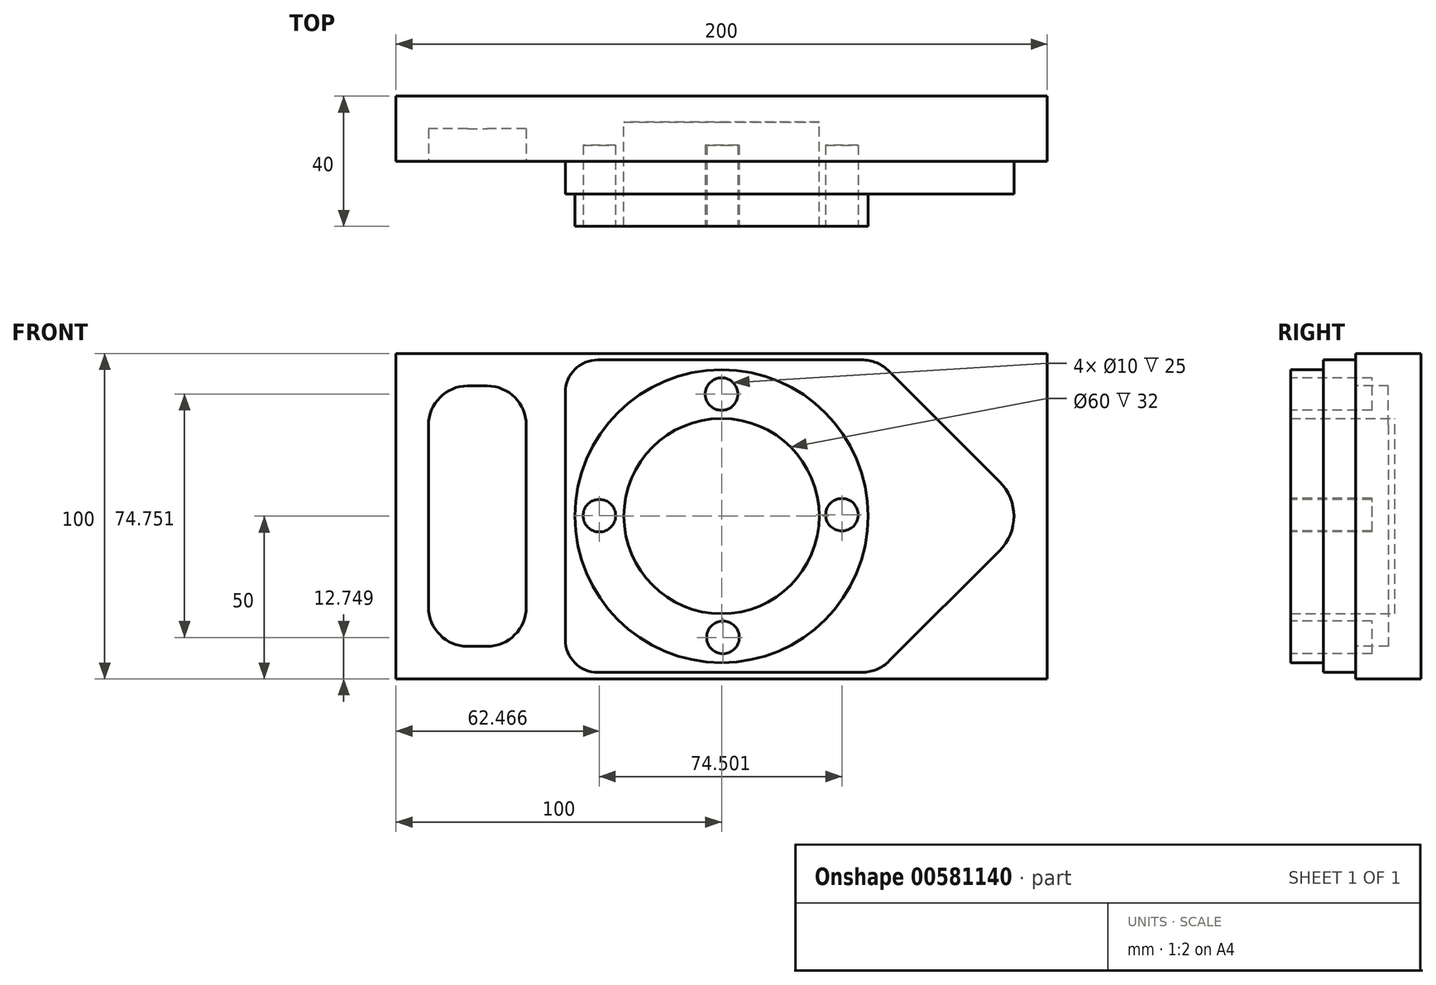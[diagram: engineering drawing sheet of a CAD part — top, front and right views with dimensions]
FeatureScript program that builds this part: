
annotation { "Feature Type Name" : "Feature", "Feature Type Description" : "" }
export const myFeature = defineFeature(function(context is Context, id is Id, definition is map)
    precondition{}
    {
        {
            var Q0;
            Q0=qCreatedBy(makeId("Front.planeOp"),FACE);
            var sketch = newSketch(context, id + "F0", { "sketchPlane" : qUnion([Q0])});
            skLineSegment(sketch, "E0.bottom", {"start": v(-100, 50) * mm, "end": v(100, 50) * mm});
            skLineSegment(sketch, "E0.top", {"start": v(-100, -50) * mm, "end": v(100, -50) * mm});
            skLineSegment(sketch, "E0.left", {"start": v(-100, 50) * mm, "end": v(-100, -50) * mm});
            skLineSegment(sketch, "E0.right", {"start": v(100, 50) * mm, "end": v(100, -50) * mm});
            skPoint(sketch, "E0.middle", {"position": v(0, 0) * mm});
            skSolve(sketch);
        }
        {
            var Q0;
            Q0=makeQuery(id+"F0.imprint","IMPRINT",FACE,{"disambiguationData":[TD([[makeQuery(id+"F0.imprint","IMPRINT",EDGE,{"derivedFrom":sQuery(id+"F0.wireOp",EDGE,"E0.bottom")}),-1.0]])]});
            extrude(context, id + "F1", {"entities" : qUnion([Q0]), "depth" : 20 * mm, "offsetDistance" : 25 * mm});
        }
        {
            var Q0;
            Q0=makeQuery(id+"F1.opExtrude","CAP_FACE",FACE,{"disambiguationData":[OSD([sQuery(id+"F0.wireOp",EDGE,"E0.bottom"),sQuery(id+"F0.wireOp",EDGE,"E0.top"),sQuery(id+"F0.wireOp",EDGE,"E0.left"),sQuery(id+"F0.wireOp",EDGE,"E0.right")])],"isStart":false});
            var sketch = newSketch(context, id + "F2", { "sketchPlane" : qUnion([Q0])});
            skLineSegment(sketch, "E1.bottom", {"start": v(-78, 40) * mm, "end": v(-72, 40) * mm});
            skLineSegment(sketch, "E1.top", {"start": v(-78, -40) * mm, "end": v(-72, -40) * mm});
            skLineSegment(sketch, "E1.left", {"start": v(-90, 28) * mm, "end": v(-90, -28) * mm});
            skLineSegment(sketch, "E1.right", {"start": v(-60, 28) * mm, "end": v(-60, -28) * mm});
            skPoint(sketch, "E1.middle", {"position": v(-75, 0) * mm});
            skPoint(sketch, "E2.visualSharp", {"position": v(-90, 40) * mm});
            skArc(sketch, "E2.filletArc", {"start": v(-78, 40) * mm, "mid": v(-86.49, 36.49) * mm, "end": v(-90, 28) * mm});
            skPoint(sketch, "E3.visualSharp", {"position": v(-60, 40) * mm});
            skArc(sketch, "E3.filletArc", {"start": v(-60, 28) * mm, "mid": v(-63.51, 36.49) * mm, "end": v(-72, 40) * mm});
            skPoint(sketch, "E4.visualSharp", {"position": v(-60, -40) * mm});
            skArc(sketch, "E4.filletArc", {"start": v(-72, -40) * mm, "mid": v(-63.51, -36.49) * mm, "end": v(-60, -28) * mm});
            skPoint(sketch, "E5.visualSharp", {"position": v(-90, -40) * mm});
            skArc(sketch, "E5.filletArc", {"start": v(-90, -28) * mm, "mid": v(-86.49, -36.49) * mm, "end": v(-78, -40) * mm});
            skSolve(sketch);
        }
        {
            var Q0;
            Q0=makeQuery(id+"F2.imprint","IMPRINT",FACE,{"disambiguationData":[TD([[makeQuery(id+"F2.imprint","IMPRINT",EDGE,{"derivedFrom":sQuery(id+"F2.wireOp",EDGE,"E1.bottom")}),-1.0]])]});
            extrude(context, id + "F3", {"entities" : qUnion([Q0]), "operationType" : NewBodyOperationType.REMOVE, "oppositeDirection" : true, "depth" : 10 * mm, "offsetDistance" : 25 * mm});
        }
        {
            var Q0;
            Q0=makeQuery(id+"F1.opExtrude","CAP_FACE",FACE,{"disambiguationData":[OSD([sQuery(id+"F0.wireOp",EDGE,"E0.bottom"),sQuery(id+"F0.wireOp",EDGE,"E0.top"),sQuery(id+"F0.wireOp",EDGE,"E0.left"),sQuery(id+"F0.wireOp",EDGE,"E0.right")])],"isStart":false});
            var sketch = newSketch(context, id + "F4", { "sketchPlane" : qUnion([Q0])});
            skLineSegment(sketch, "E6.bottom", {"start": v(43.03, -48) * mm, "end": v(-38, -48) * mm});
            skLineSegment(sketch, "E6.top", {"start": v(43.03, 48) * mm, "end": v(-38, 48) * mm});
            skLineSegment(sketch, "E6.right", {"start": v(-48, -38) * mm, "end": v(-48, 38) * mm});
            skPoint(sketch, "E6.middle", {"position": v(0, 0) * mm});
            skPoint(sketch, "E7.visualSharp", {"position": v(-48, 48) * mm});
            skArc(sketch, "E7.filletArc", {"start": v(-38, 48) * mm, "mid": v(-45.07, 45.07) * mm, "end": v(-48, 38) * mm});
            skPoint(sketch, "E8.visualSharp", {"position": v(-48, -48) * mm});
            skArc(sketch, "E8.filletArc", {"start": v(-48, -38) * mm, "mid": v(-45.07, -45.07) * mm, "end": v(-38, -48) * mm});
            skLineSegment(sketch, "E9", {"start": v(51.51, 44.48) * mm, "end": v(85.4, 10.6) * mm});
            skLineSegment(sketch, "E10", {"start": v(85.4, -10.6) * mm, "end": v(51.51, -44.48) * mm});
            skPoint(sketch, "E11.visualSharp", {"position": v(96, 0) * mm});
            skArc(sketch, "E11.filletArc", {"start": v(85.4, -10.6) * mm, "mid": v(89.78, 0) * mm, "end": v(85.4, 10.6) * mm});
            skPoint(sketch, "E12.visualSharp", {"position": v(48, 48) * mm});
            skArc(sketch, "E12.filletArc", {"start": v(51.51, 44.48) * mm, "mid": v(47.62, 47.09) * mm, "end": v(43.03, 48) * mm});
            skPoint(sketch, "E13.visualSharp", {"position": v(48, -48) * mm});
            skArc(sketch, "E13.filletArc", {"start": v(43.03, -48) * mm, "mid": v(47.62, -47.09) * mm, "end": v(51.51, -44.48) * mm});
            skSolve(sketch);
        }
        {
            var Q0;
            Q0=makeQuery(id+"F4.imprint","IMPRINT",FACE,{"disambiguationData":[TD([[makeQuery(id+"F4.imprint","IMPRINT",EDGE,{"derivedFrom":sQuery(id+"F4.wireOp",EDGE,"E6.bottom")}),-1.0]])]});
            extrude(context, id + "F5", {"entities" : qUnion([Q0]), "operationType" : NewBodyOperationType.ADD, "depth" : 10 * mm, "offsetDistance" : 25 * mm});
        }
        {
            var Q0;
            Q0=makeQuery(id+"F5.opExtrude","CAP_FACE",FACE,{"disambiguationData":[OSD([sQuery(id+"F4.wireOp",EDGE,"E6.bottom"),sQuery(id+"F4.wireOp",EDGE,"E6.top"),sQuery(id+"F4.wireOp",EDGE,"E6.right"),sQuery(id+"F4.wireOp",EDGE,"E7.filletArc"),sQuery(id+"F4.wireOp",EDGE,"E8.filletArc"),sQuery(id+"F4.wireOp",EDGE,"E9"),sQuery(id+"F4.wireOp",EDGE,"E10"),sQuery(id+"F4.wireOp",EDGE,"E11.filletArc"),sQuery(id+"F4.wireOp",EDGE,"E12.filletArc"),sQuery(id+"F4.wireOp",EDGE,"E13.filletArc")])],"isStart":false});
            var sketch = newSketch(context, id + "F6", { "sketchPlane" : qUnion([Q0])});
            skCircle(sketch, "E14", {"center": v(0, 0) * mm, "radius": 45 * mm});
            skCircle(sketch, "E15", {"center": v(0, 0) * mm, "radius": 30 * mm});
            skSolve(sketch);
        }
        {
            var Q0;
            Q0=makeQuery(id+"F6.imprint","IMPRINT",FACE,{"disambiguationData":[TD([[makeQuery(id+"F6.imprint","IMPRINT",EDGE,{"derivedFrom":sQuery(id+"F6.wireOp",EDGE,"E14")}),1.0]])]});
            extrude(context, id + "F7", {"entities" : qUnion([Q0]), "operationType" : NewBodyOperationType.ADD, "depth" : 10 * mm, "offsetDistance" : 25 * mm});
        }
        {
            var Q0;
            Q0=makeQuery(id+"F7.opExtrude","CAP_FACE",FACE,{"disambiguationData":[OSD([sQuery(id+"F6.wireOp",EDGE,"E14"),sQuery(id+"F6.wireOp",EDGE,"E15")])],"isStart":false});
            var sketch = newSketch(context, id + "F8", { "sketchPlane" : qUnion([Q0])});
            skCircle(sketch, "E16", {"center": v(0, 0) * mm, "radius": 37.5 * mm, "construction": true});
            skCircle(sketch, "E17", {"center": v(0, 37.5) * mm, "radius": 5 * mm});
            skCircle(sketch, "E18", {"center": v(0.42, -37.25) * mm, "radius": 5 * mm});
            skCircle(sketch, "E19", {"center": v(36.97, 0.42) * mm, "radius": 5 * mm});
            skCircle(sketch, "E20", {"center": v(-37.53, 0.14) * mm, "radius": 5 * mm});
            skSolve(sketch);
        }
        {
            var Q0;
            Q0=makeQuery(id+"F8.imprint","IMPRINT",FACE,{"disambiguationData":[TD([[makeQuery(id+"F8.imprint","IMPRINT",EDGE,{"derivedFrom":sQuery(id+"F8.wireOp",EDGE,"E20")}),1.0]])]});
            var Q1;
            Q1=makeQuery(id+"F8.imprint","IMPRINT",FACE,{"disambiguationData":[TD([[makeQuery(id+"F8.imprint","IMPRINT",EDGE,{"derivedFrom":sQuery(id+"F8.wireOp",EDGE,"E19")}),1.0]])]});
            var Q2;
            Q2=makeQuery(id+"F8.imprint","IMPRINT",FACE,{"disambiguationData":[TD([[makeQuery(id+"F8.imprint","IMPRINT",EDGE,{"derivedFrom":sQuery(id+"F8.wireOp",EDGE,"E17")}),1.0]])]});
            var Q3;
            Q3=makeQuery(id+"F8.imprint","IMPRINT",FACE,{"disambiguationData":[TD([[makeQuery(id+"F8.imprint","IMPRINT",EDGE,{"derivedFrom":sQuery(id+"F8.wireOp",EDGE,"E18")}),1.0]])]});
            extrude(context, id + "F9", {"entities" : qUnion([Q0, Q1, Q2, Q3]), "operationType" : NewBodyOperationType.REMOVE, "oppositeDirection" : true, "depth" : 25 * mm, "offsetDistance" : 25 * mm});
        }
        {
            var Q0;
            Q0=makeQuery(id+"F7.boolean.opBoolean","SPLIT",FACE,{"disambiguationData":[TD([makeQuery(id+"F7.opExtrude","SWEPT_FACE",FACE,{"disambiguationData":[OSD([sQuery(id+"F6.wireOp",EDGE,"E15")])]})])],"derivedFrom":makeQuery(id+"F5.opExtrude","CAP_FACE",FACE,{"disambiguationData":[OSD([sQuery(id+"F4.wireOp",EDGE,"E6.bottom"),sQuery(id+"F4.wireOp",EDGE,"E6.top"),sQuery(id+"F4.wireOp",EDGE,"E6.right"),sQuery(id+"F4.wireOp",EDGE,"E7.filletArc"),sQuery(id+"F4.wireOp",EDGE,"E8.filletArc"),sQuery(id+"F4.wireOp",EDGE,"E9"),sQuery(id+"F4.wireOp",EDGE,"E10"),sQuery(id+"F4.wireOp",EDGE,"E11.filletArc"),sQuery(id+"F4.wireOp",EDGE,"E12.filletArc"),sQuery(id+"F4.wireOp",EDGE,"E13.filletArc")])],"isStart":false})});
            var sketch = newSketch(context, id + "F10", { "sketchPlane" : qUnion([Q0])});
            skCircle(sketch, "E21", {"center": v(0, 0) * mm, "radius": 30 * mm});
            skSolve(sketch);
        }
        {
            var Q0;
            Q0=makeQuery(id+"F10.imprint","IMPRINT",FACE,{"disambiguationData":[TD([[makeQuery(id+"F10.imprint","IMPRINT",EDGE,{"derivedFrom":sQuery(id+"F10.wireOp",EDGE,"E21")}),1.0]])]});
            extrude(context, id + "F11", {"entities" : qUnion([Q0]), "operationType" : NewBodyOperationType.REMOVE, "oppositeDirection" : true, "depth" : 22 * mm, "offsetDistance" : 25 * mm});
        }
    });
